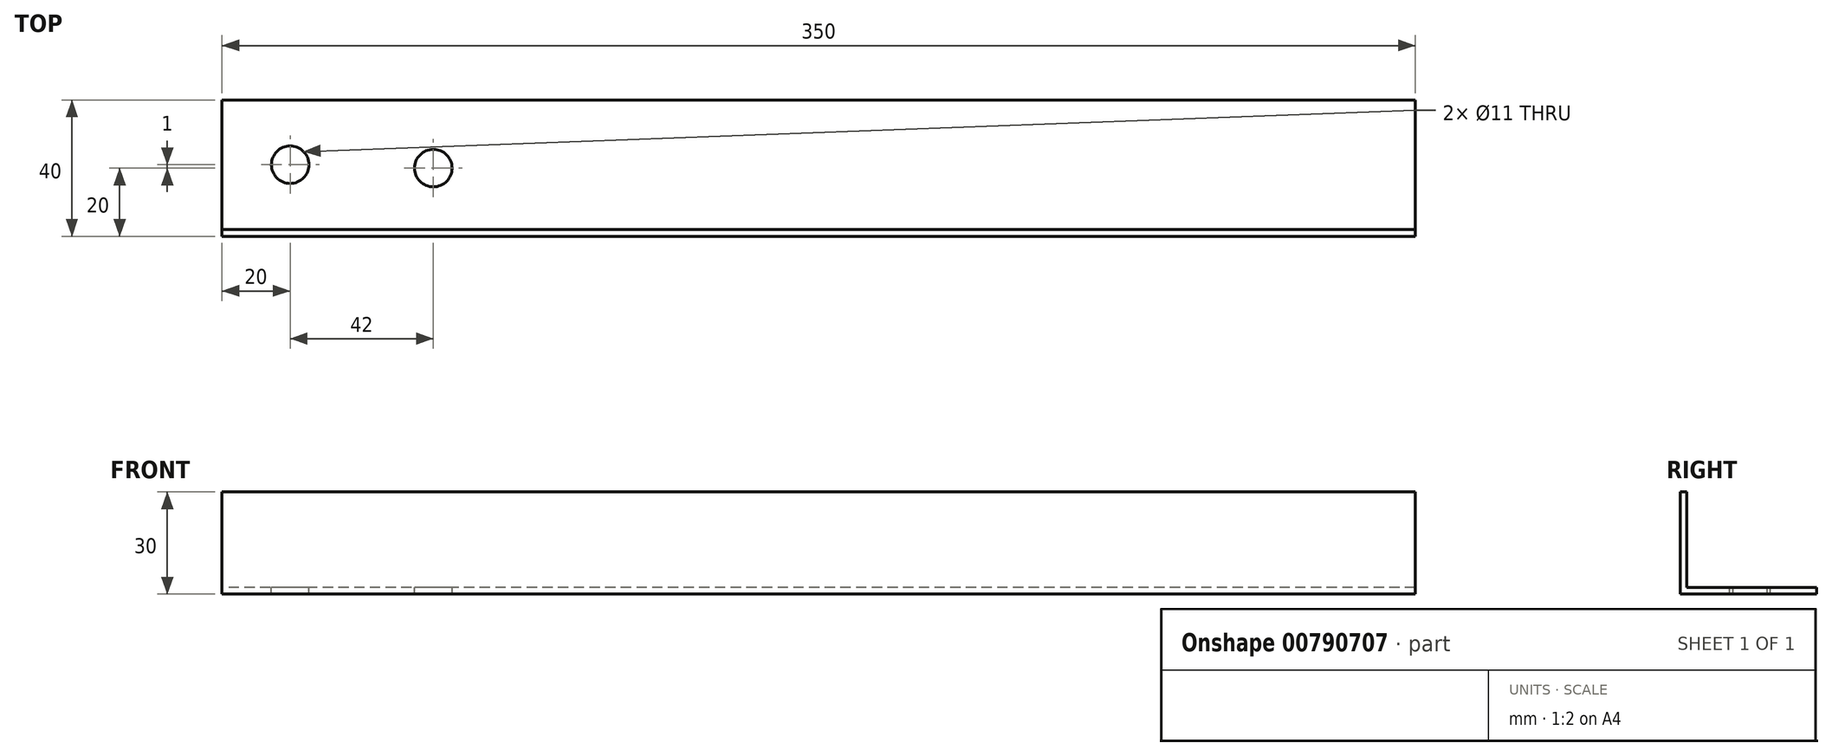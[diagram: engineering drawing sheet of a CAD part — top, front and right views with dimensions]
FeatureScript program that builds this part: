
annotation { "Feature Type Name" : "Feature", "Feature Type Description" : "" }
export const myFeature = defineFeature(function(context is Context, id is Id, definition is map)
    precondition{}
    {
        {
            var Q0;
            Q0=qCreatedBy(makeId("Right.planeOp"),FACE);
            var sketch = newSketch(context, id + "F0", { "sketchPlane" : qUnion([Q0])});
            skLineSegment(sketch, "E0", {"start": v(0, 0) * mm, "end": v(0, 30) * mm});
            skLineSegment(sketch, "E1", {"start": v(0, 0) * mm, "end": v(40, 0) * mm});
            skLineSegment(sketch, "E2.0", {"start": v(2, 2) * mm, "end": v(40, 2) * mm});
            skLineSegment(sketch, "E2.1", {"start": v(2, 2) * mm, "end": v(2, 30) * mm});
            skLineSegment(sketch, "E3", {"start": v(0, 30) * mm, "end": v(2, 30) * mm});
            skLineSegment(sketch, "E4", {"start": v(40, 0) * mm, "end": v(40, 2) * mm});
            skSolve(sketch);
        }
        {
            var Q0;
            Q0=makeQuery(id+"F0.imprint","IMPRINT",FACE,{"disambiguationData":[TD([[makeQuery(id+"F0.imprint","IMPRINT",EDGE,{"derivedFrom":sQuery(id+"F0.wireOp",EDGE,"E0")}),-1.0]])]});
            extrude(context, id + "F1", {"entities" : qUnion([Q0]), "depth" : 350 * mm, "offsetDistance" : 25 * mm});
        }
        {
            var Q0;
            Q0=makeQuery(id+"F1.opExtrude","SWEPT_FACE",FACE,{"disambiguationData":[OSD([sQuery(id+"F0.wireOp",EDGE,"E2.0")])]});
            var sketch = newSketch(context, id + "F2", { "sketchPlane" : qUnion([Q0])});
            skCircle(sketch, "E5", {"center": v(20, 21) * mm, "radius": 5.5 * mm});
            skPoint(sketch, "E5.centerSnap0", {"position": v(0, 21) * mm});
            skCircle(sketch, "E6", {"center": v(62, 20) * mm, "radius": 5.5 * mm});
            skSolve(sketch);
        }
        {
            var Q0;
            Q0=makeQuery(id+"F2.imprint","IMPRINT",FACE,{"disambiguationData":[TD([[makeQuery(id+"F2.imprint","IMPRINT",EDGE,{"derivedFrom":sQuery(id+"F2.wireOp",EDGE,"E5")}),1.0]])]});
            var Q1;
            Q1=makeQuery(id+"F2.imprint","IMPRINT",FACE,{"disambiguationData":[TD([[makeQuery(id+"F2.imprint","IMPRINT",EDGE,{"derivedFrom":sQuery(id+"F2.wireOp",EDGE,"E6")}),1.0]])]});
            extrude(context, id + "F3", {"entities" : qUnion([Q0, Q1]), "operationType" : NewBodyOperationType.REMOVE, "oppositeDirection" : true, "depth" : 25 * mm, "offsetDistance" : 25 * mm});
        }
    });
